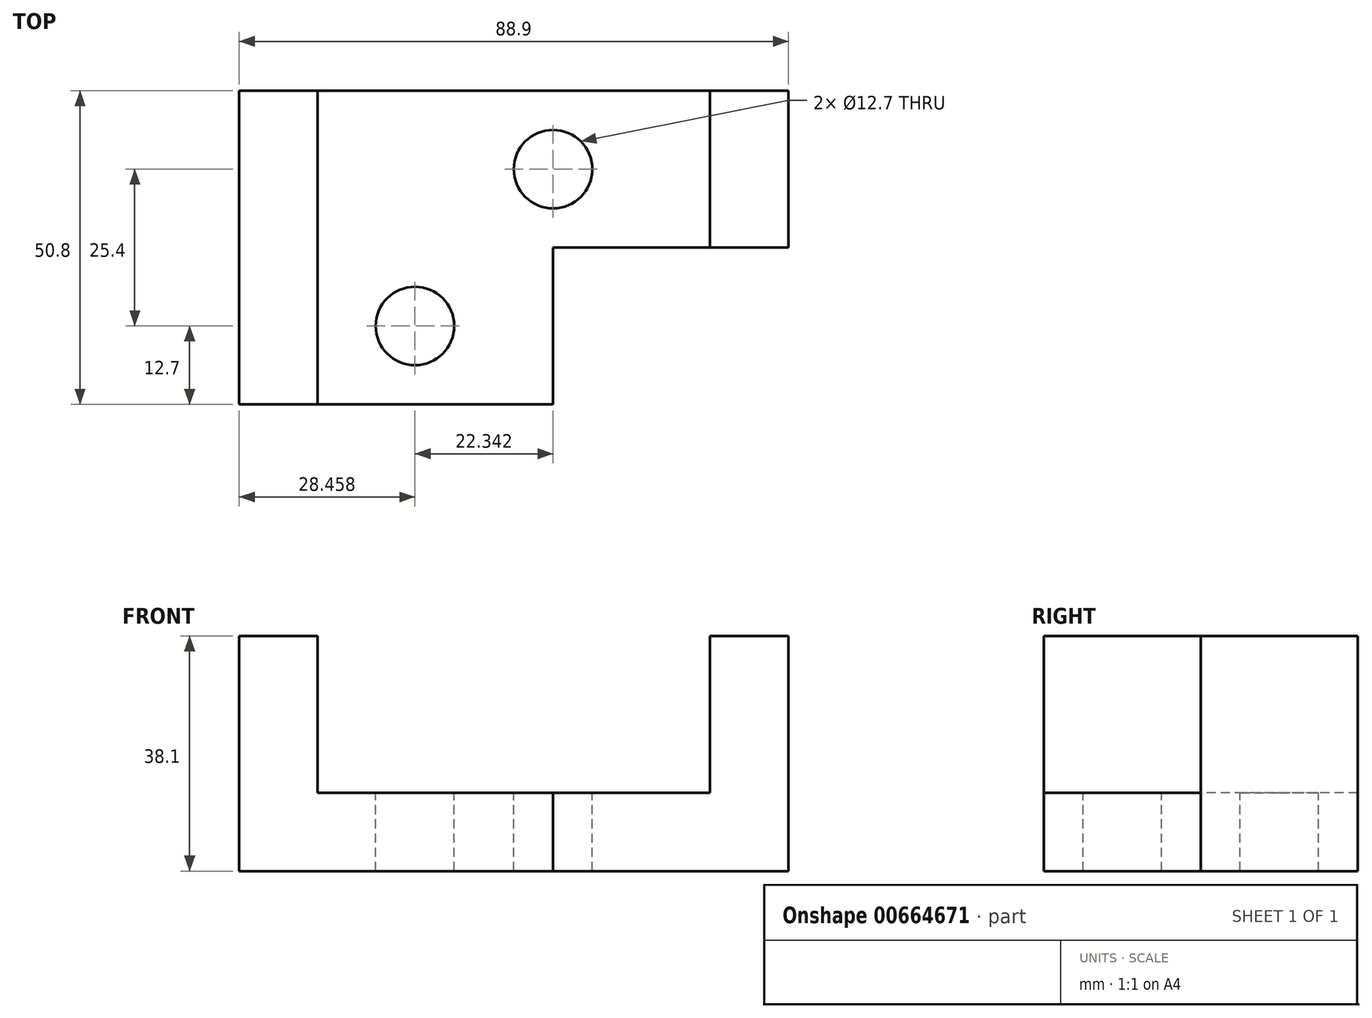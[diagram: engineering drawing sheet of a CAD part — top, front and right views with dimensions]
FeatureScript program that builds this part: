
annotation { "Feature Type Name" : "Feature", "Feature Type Description" : "" }
export const myFeature = defineFeature(function(context is Context, id is Id, definition is map)
    precondition{}
    {
        {
            var Q0;
            Q0=qCreatedBy(makeId("Front.planeOp"),FACE);
            var sketch = newSketch(context, id + "F0", { "sketchPlane" : qUnion([Q0])});
            skLineSegment(sketch, "E0.bottom", {"start": v(44.45, 19.05) * mm, "end": v(-44.45, 19.05) * mm});
            skLineSegment(sketch, "E0.top", {"start": v(44.45, -19.05) * mm, "end": v(-44.45, -19.05) * mm});
            skLineSegment(sketch, "E0.left", {"start": v(44.45, 19.05) * mm, "end": v(44.45, -19.05) * mm});
            skLineSegment(sketch, "E0.right", {"start": v(-44.45, 19.05) * mm, "end": v(-44.45, -19.05) * mm});
            skPoint(sketch, "E0.middle", {"position": v(0, 0) * mm});
            skSolve(sketch);
        }
        {
            var Q0;
            Q0 = qSketchRegion(id + "F0", true);
            extrude(context, id + "F1", {"entities" : qUnion([Q0]), "depth" : 50.8 * mm, "offsetDistance" : 25.4 * mm});
        }
        {
            var Q0;
            Q0=makeQuery(id+"F1.opExtrude","CAP_FACE",FACE,{"disambiguationData":[OSD([sQuery(id+"F0.wireOp",EDGE,"E0.bottom"),sQuery(id+"F0.wireOp",EDGE,"E0.top"),sQuery(id+"F0.wireOp",EDGE,"E0.left"),sQuery(id+"F0.wireOp",EDGE,"E0.right")])],"isStart":false});
            var sketch = newSketch(context, id + "F2", { "sketchPlane" : qUnion([Q0])});
            skLineSegment(sketch, "E1.bottom", {"start": v(-31.75, 19.05) * mm, "end": v(31.75, 19.05) * mm});
            skLineSegment(sketch, "E1.top", {"start": v(-31.75, -6.35) * mm, "end": v(31.75, -6.35) * mm});
            skLineSegment(sketch, "E1.left", {"start": v(-31.75, 19.05) * mm, "end": v(-31.75, -6.35) * mm});
            skLineSegment(sketch, "E1.right", {"start": v(31.75, 19.05) * mm, "end": v(31.75, -6.35) * mm});
            skSolve(sketch);
        }
        {
            var Q0;
            Q0 = qSketchRegion(id + "F2", true);
            extrude(context, id + "F3", {"entities" : qUnion([Q0]), "operationType" : NewBodyOperationType.REMOVE, "endBound" : BoundingType.THROUGH_ALL, "oppositeDirection" : true, "depth" : 50.8 * mm, "offsetDistance" : 25.4 * mm});
        }
        {
            var Q0;
            {var subQ1=sQuery(id+"F0.wireOp",EDGE,"E0.left");var subQ3=sQuery(id+"F0.wireOp",EDGE,"E0.bottom");Q0=makeQuery(id+"F3.boolean.opBoolean","SPLIT",FACE,{"disambiguationData":[TD([makeQuery(id+"F1.opExtrude","SWEPT_FACE",FACE,{"disambiguationData":[OSD([subQ1])]})])],"derivedFrom":makeQuery(id+"F1.opExtrude","SWEPT_FACE",FACE,{"disambiguationData":[OSD([subQ3])]})});}
            var sketch = newSketch(context, id + "F4", { "sketchPlane" : qUnion([Q0])});
            skLineSegment(sketch, "E2.bottom", {"start": v(44.45, -50.8) * mm, "end": v(6.35, -50.8) * mm});
            skLineSegment(sketch, "E2.top", {"start": v(44.45, -25.4) * mm, "end": v(6.35, -25.4) * mm});
            skLineSegment(sketch, "E2.left", {"start": v(44.45, -50.8) * mm, "end": v(44.45, -25.4) * mm});
            skLineSegment(sketch, "E2.right", {"start": v(6.35, -50.8) * mm, "end": v(6.35, -25.4) * mm});
            skSolve(sketch);
        }
        {
            var Q0;
            Q0 = qSketchRegion(id + "F4", true);
            extrude(context, id + "F5", {"entities" : qUnion([Q0]), "operationType" : NewBodyOperationType.REMOVE, "endBound" : BoundingType.THROUGH_ALL, "oppositeDirection" : true, "depth" : 25.4 * mm, "offsetDistance" : 25.4 * mm});
        }
        {
            var Q0;
            Q0=makeQuery(id+"F3.boolean.opBoolean","COPY",FACE,{"derivedFrom":makeQuery(id+"F3.opExtrude","SWEPT_FACE",FACE,{"disambiguationData":[OSD([sQuery(id+"F2.wireOp",EDGE,"E1.top")])]})});
            var sketch = newSketch(context, id + "F6", { "sketchPlane" : qUnion([Q0])});
            skCircle(sketch, "E3", {"center": v(-16, -38.1) * mm, "radius": 6.35 * mm});
            skSolve(sketch);
        }
        {
            var Q0;
            Q0 = qSketchRegion(id + "F6", true);
            extrude(context, id + "F7", {"entities" : qUnion([Q0]), "operationType" : NewBodyOperationType.REMOVE, "endBound" : BoundingType.THROUGH_ALL, "oppositeDirection" : true, "depth" : 25.4 * mm, "offsetDistance" : 25.4 * mm});
        }
        {
            var Q0;
            Q0=makeQuery(id+"F3.boolean.opBoolean","COPY",FACE,{"derivedFrom":makeQuery(id+"F3.opExtrude","SWEPT_FACE",FACE,{"disambiguationData":[OSD([sQuery(id+"F2.wireOp",EDGE,"E1.top")])]})});
            var sketch = newSketch(context, id + "F8", { "sketchPlane" : qUnion([Q0])});
            skCircle(sketch, "E4", {"center": v(6.35, -12.7) * mm, "radius": 6.35 * mm});
            skSolve(sketch);
        }
        {
            var Q0;
            Q0 = qSketchRegion(id + "F8", true);
            extrude(context, id + "F9", {"entities" : qUnion([Q0]), "operationType" : NewBodyOperationType.REMOVE, "endBound" : BoundingType.THROUGH_ALL, "oppositeDirection" : true, "depth" : 25.4 * mm, "offsetDistance" : 25.4 * mm});
        }
    });
